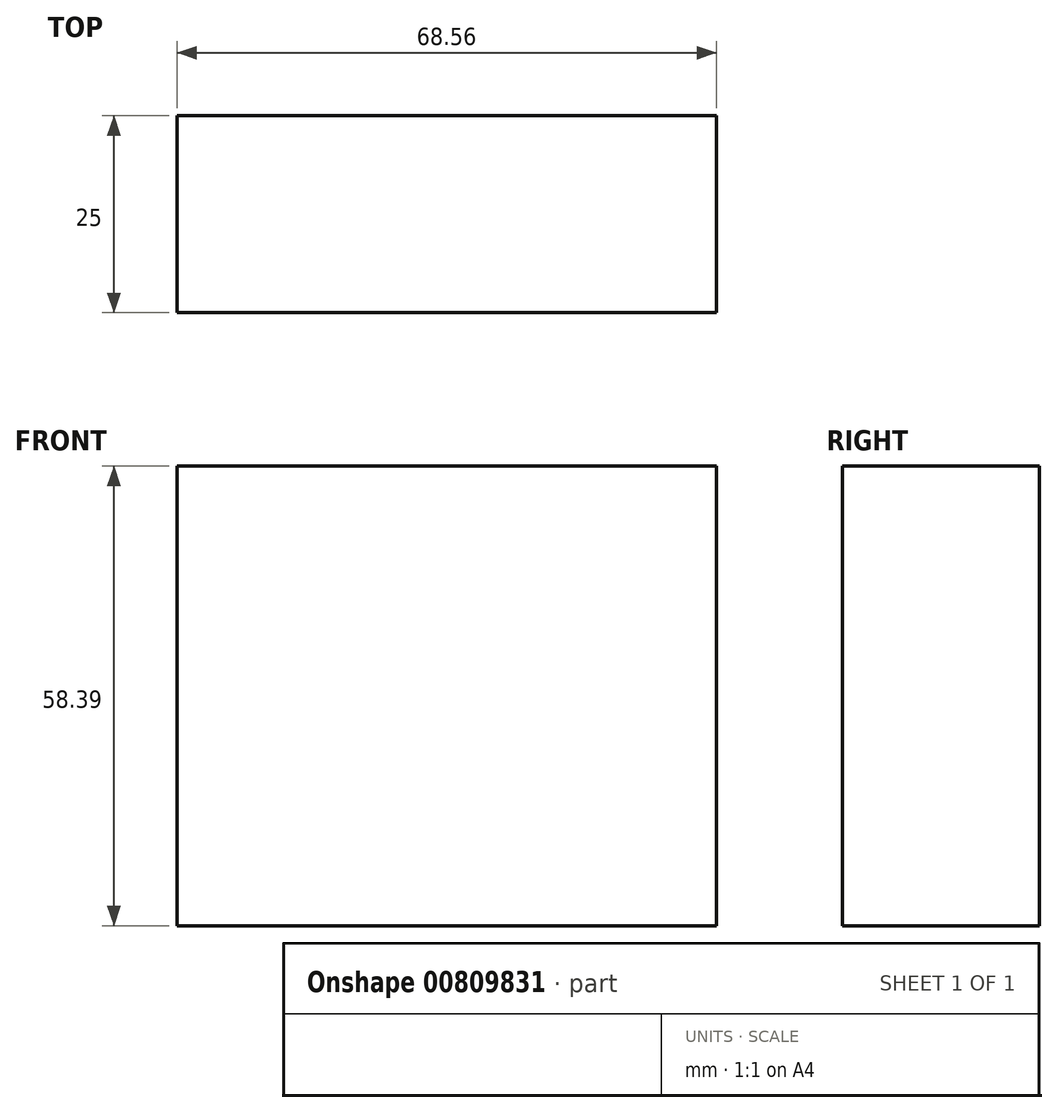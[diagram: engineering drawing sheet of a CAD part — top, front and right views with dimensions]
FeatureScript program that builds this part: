
annotation { "Feature Type Name" : "Feature", "Feature Type Description" : "" }
export const myFeature = defineFeature(function(context is Context, id is Id, definition is map)
    precondition{}
    {
        {
            var Q0;
            Q0=qCreatedBy(makeId("Front.planeOp"),FACE);
            var sketch = newSketch(context, id + "F0", { "sketchPlane" : qUnion([Q0])});
            skLineSegment(sketch, "E0.bottom", {"start": v(-29.84, 62.34) * mm, "end": v(38.72, 62.34) * mm});
            skLineSegment(sketch, "E0.top", {"start": v(-29.84, 28.95) * mm, "end": v(38.72, 28.95) * mm});
            skLineSegment(sketch, "E0.left", {"start": v(-29.84, 62.34) * mm, "end": v(-29.84, 28.95) * mm});
            skLineSegment(sketch, "E0.right", {"start": v(38.72, 62.34) * mm, "end": v(38.72, 28.95) * mm});
            skSolve(sketch);
        }
        {
            var Q0;
            Q0 = qSketchRegion(id + "F0", true);
            extrude(context, id + "F1", {"entities" : qUnion([Q0]), "depth" : 25 * mm, "offsetDistance" : 25 * mm});
        }
        {
            var Q0;
            Q0=makeQuery(id+"F1.opExtrude","SWEPT_FACE",FACE,{"disambiguationData":[OSD([sQuery(id+"F0.wireOp",EDGE,"E0.bottom")])]});
            extrude(context, id + "F2", {"entities" : qUnion([Q0]), "operationType" : NewBodyOperationType.ADD, "depth" : 25 * mm, "offsetDistance" : 25 * mm});
        }
        {
            var Q0;
            {var subQ0=sQuery(id+"F0.wireOp",EDGE,"E0.bottom");Q0=makeQuery(id+"F2.boolean.opBoolean","MERGE",FACE,{"derivedFrom":[makeQuery(id+"F1.opExtrude","CAP_FACE",FACE,{"disambiguationData":[OSD([subQ0,sQuery(id+"F0.wireOp",EDGE,"E0.top"),sQuery(id+"F0.wireOp",EDGE,"E0.left"),sQuery(id+"F0.wireOp",EDGE,"E0.right")])],"isStart":false}),makeQuery(id+"F2.opExtrude","SWEPT_FACE",FACE,{"disambiguationData":[OSD([subQ0]),TDD([makeQuery(id+"F1.opExtrude","CAP_EDGE",EDGE,{"disambiguationData":[OSD([subQ0])],"isStart":false})])]})]});}
            cPlane(context, id + "F3", {"entities" : qUnion([Q0]), "cplaneType" : CPlaneType.OFFSET, "offset" : 79.34 * mm, "width" : 150 * mm, "height" : 150 * mm});
        }
    });
